# Revit family: FA_ЗажимСоединенительный_Пруток_Стержень_EZETEK
name_source: partatom
category: Системы пожарной сигнализации
revit_build: Autodesk Revit 2017 (Build: 20170118_1100(x64)
units: mm (PartAtom-declared; Revit-internal decimal feet)

## family parameters
Всегда вертикально = Да
На основе рабочей плоскости = Нет
Общий = Нет
При загрузке вырезать с полостями = Нет
Размер круглого соединителя = Использовать радиус
Сохранять ориентацию аннотаций = Нет
Тип детали = Нормальный
Точка расчета площади = Нет

## types (3) — shared parameters
ADSK_Версия Revit = 2017
ADSK_Единица измерения = шт.
ADSK_Завод-изготовитель = Ezetek
ADSK_Количество = 1
ADSK_Масса = 0.053
ADSK_Масса_Текст = 0.053
URL = https://ezetek.ru
Группа модели = Зажимы заземления
Изготовитель = Ezetek
Описание = Зажим соединение прутка и стержня осуществляется затяжкой болта. Болт имеет резьбу М10.

## per-type parameters (varying)
| type | ADSK_Код изделия | ADSK_Марка | ADSK_Материал | ADSK_Наименование | ADSK_Обозначение |
| ЗажимСоединенительный_Пруток_Стержень_Медь_90554 | 90554 | 90554 | BIMLIB_Медь_EZETEK | Зажим соединительный пруток — стержень, медь | 90554 |
| ЗажимСоединенительный_Пруток_Стержень_Латунь_90555 | 90555 | 90555 | BIMLIB_Латунь_EZETEK | Зажим соединительный пруток — стержень, латунь | 90555 |
| ЗажимСоединенительный_Пруток_Стержень_Сталь_Оцинкованная_90555 | 90551 | 90551 | BIMLIB_Сталь_Оцинкованная_EZETEK | Зажим соединительный пруток — стержень, оцинк. | 90551 |
